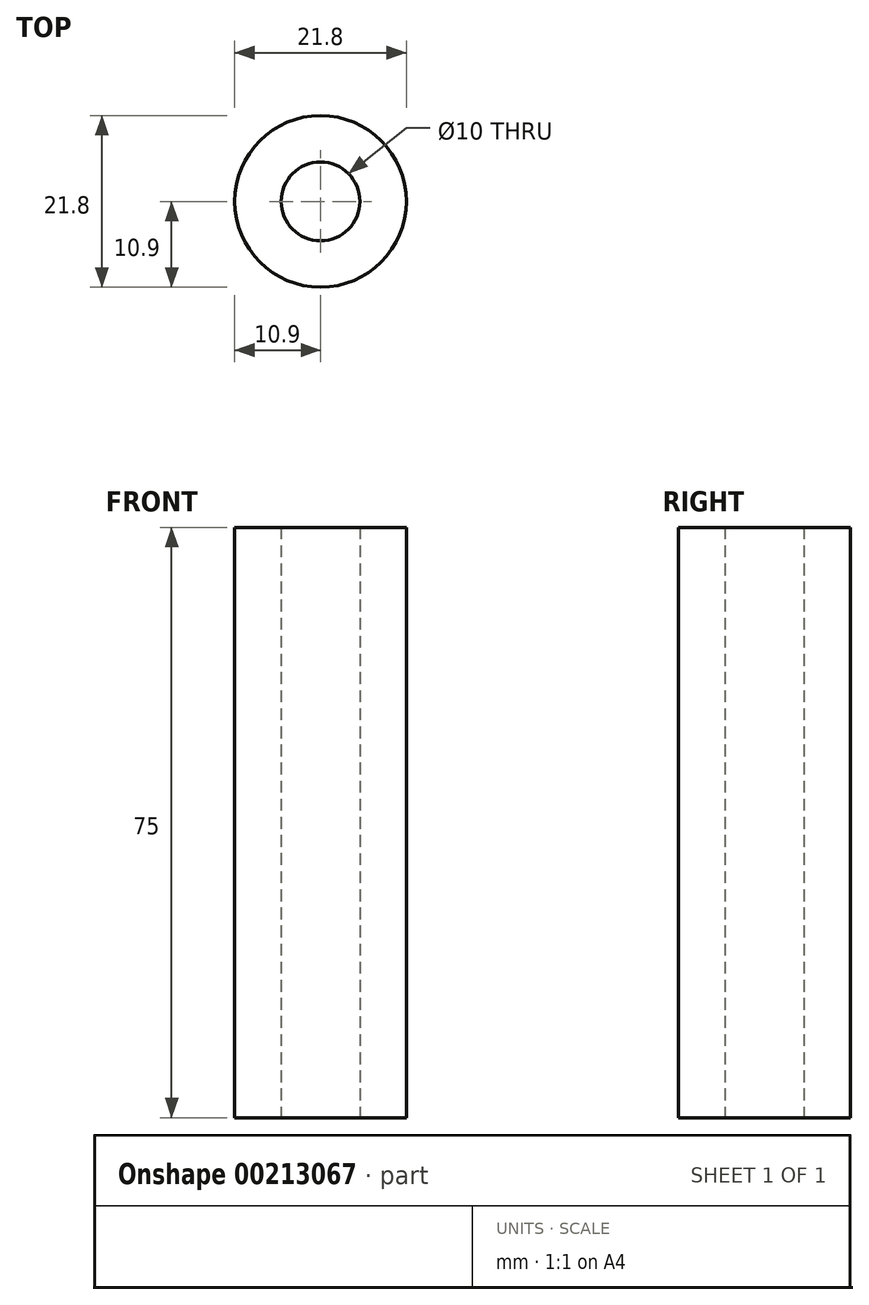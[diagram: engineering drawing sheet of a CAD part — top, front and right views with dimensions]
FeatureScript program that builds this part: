
annotation { "Feature Type Name" : "Feature", "Feature Type Description" : "" }
export const myFeature = defineFeature(function(context is Context, id is Id, definition is map)
    precondition{}
    {
        {
            var Q0;
            Q0=qCreatedBy(makeId("Top.planeOp"),FACE);
            var sketch = newSketch(context, id + "F0", { "sketchPlane" : qUnion([Q0])});
            skCircle(sketch, "E0", {"center": v(0, 0) * mm, "radius": 10.9 * mm});
            skSolve(sketch);
        }
        {
            var Q0;
            Q0=makeQuery(id+"F0.imprint","IMPRINT",FACE,{"disambiguationData":[TD([[makeQuery(id+"F0.imprint","IMPRINT",EDGE,{"derivedFrom":sQuery(id+"F0.wireOp",EDGE,"E0")}),1.0]])]});
            extrude(context, id + "F1", {"entities" : qUnion([Q0]), "depth" : 75 * mm});
        }
        {
            var Q0;
            Q0=qCreatedBy(makeId("Top.planeOp"),FACE);
            var sketch = newSketch(context, id + "F2", { "sketchPlane" : qUnion([Q0])});
            skCircle(sketch, "E1", {"center": v(0, 0) * mm, "radius": 5 * mm});
            skSolve(sketch);
        }
        {
            var Q0;
            Q0 = qSketchRegion(id + "F2", true);
            extrude(context, id + "F3", {"entities" : qUnion([Q0]), "operationType" : NewBodyOperationType.REMOVE, "depth" : 80 * mm});
        }
    });
